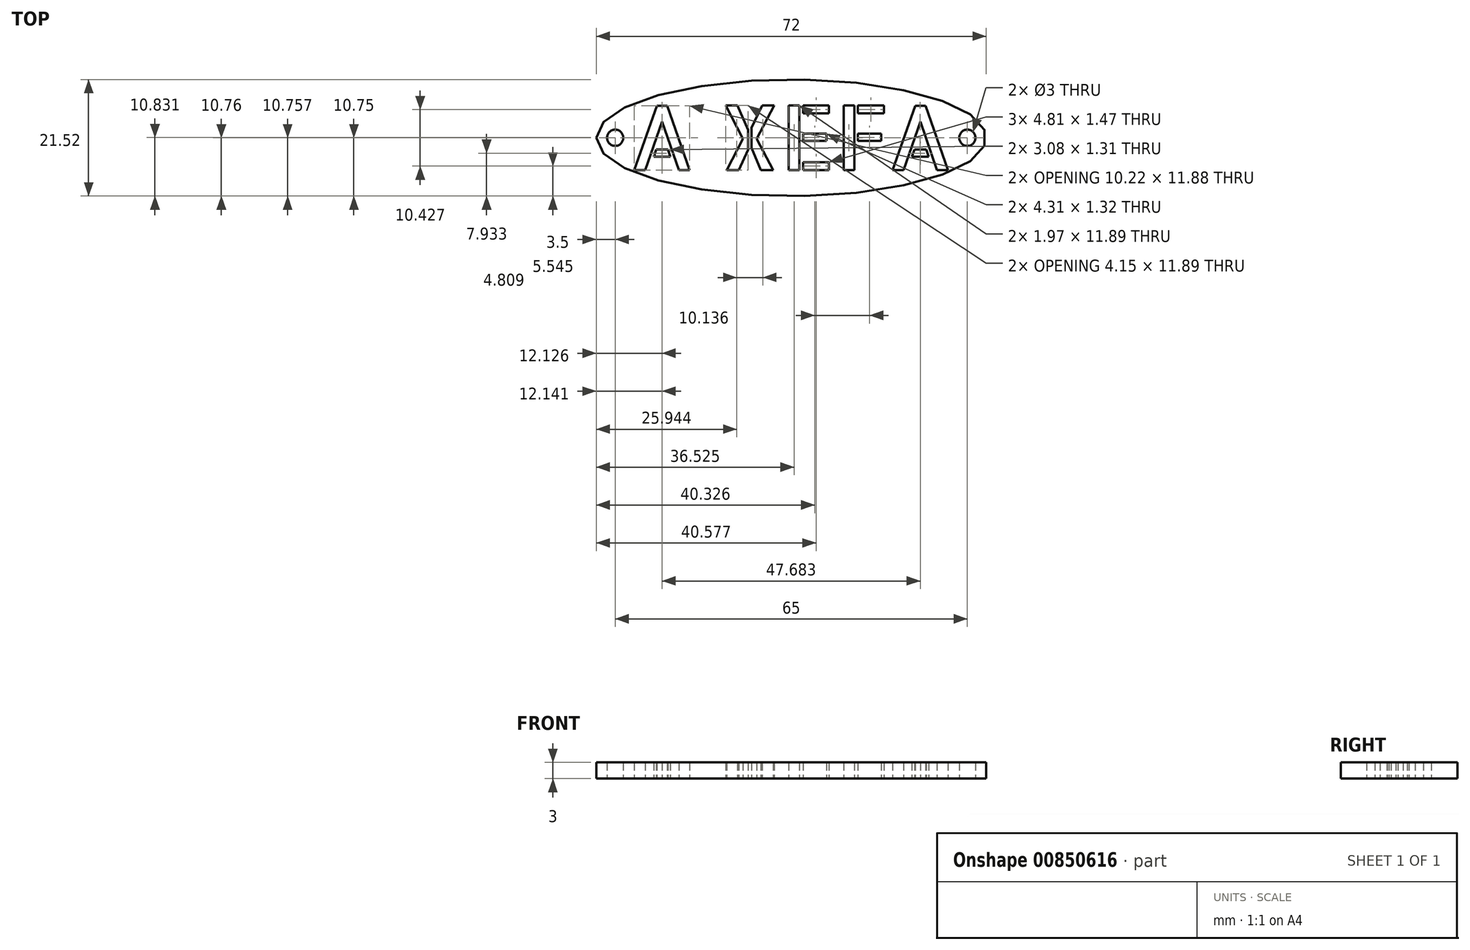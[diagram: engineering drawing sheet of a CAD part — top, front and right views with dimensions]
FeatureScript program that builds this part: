
annotation { "Feature Type Name" : "Feature", "Feature Type Description" : "" }
export const myFeature = defineFeature(function(context is Context, id is Id, definition is map)
    precondition{}
    {
        {
            var Q0;
            Q0=qCreatedBy(makeId("Top.planeOp"),FACE);
            var sketch = newSketch(context, id + "F0", { "sketchPlane" : qUnion([Q0])});
            skEllipse(sketch, "E0", {"center": v(0, 0) * mm, "majorRadius": 36 * mm, "minorRadius": 10.76 * mm, "majorAxis": v(-1, 0)});
            skCircle(sketch, "E1", {"center": v(-32.5, 0) * mm, "radius": 1.5 * mm});
            skText(sketch, "E2", { "text": "A XEFA", "fontName": "AllertaStencil-Regular.ttf"});
            skLineSegment(sketch, "E3", {"start": v(30, 0) * mm, "end": v(-30, 0) * mm, "construction": true});
            skCircle(sketch, "E4", {"center": v(32.5, 0) * mm, "radius": 1.5 * mm});
            const initialGuessF0  = {"E2": [-0.03, -0.00595, 1, 0, 0.0119]};
            skSetInitialGuess(sketch, initialGuessF0);
            skSolve(sketch);
        }
        {
            var Q0;
            Q0=makeQuery(id+"F0.imprint","IMPRINT",FACE,{"disambiguationData":[TD([[makeQuery(id+"F0.imprint","IMPRINT",EDGE,{"derivedFrom":sQuery(id+"F0.wireOp",EDGE,"E0")}),1.0]])]});
            extrude(context, id + "F1", {"entities" : qUnion([Q0]), "depth" : 3 * mm, "offsetDistance" : 25 * mm});
        }
    });
